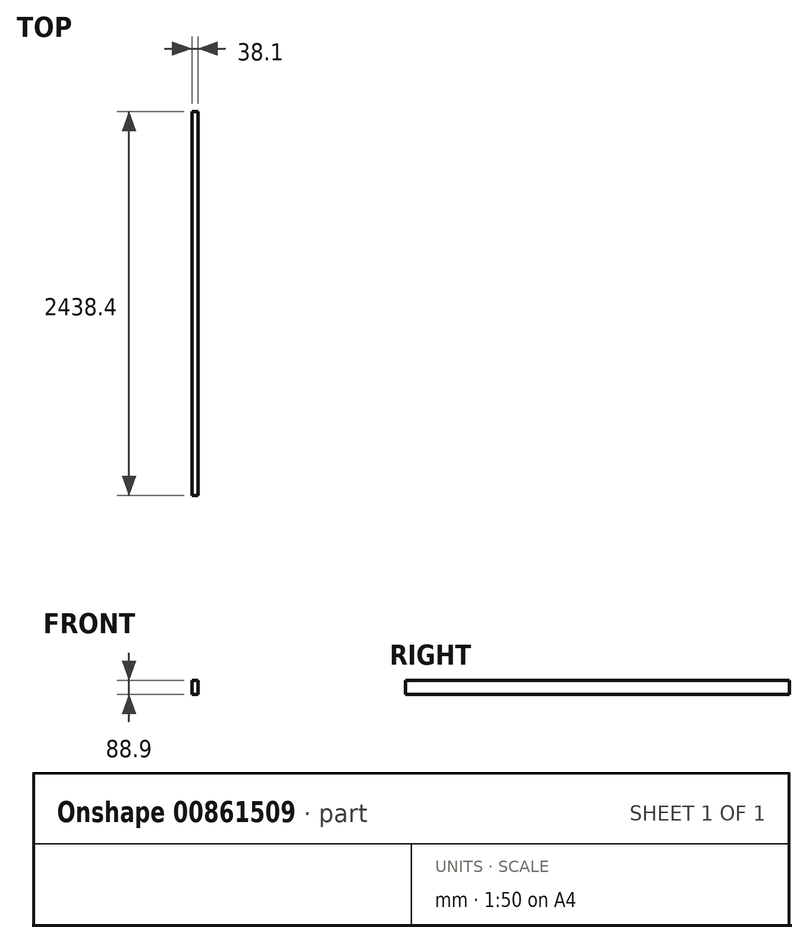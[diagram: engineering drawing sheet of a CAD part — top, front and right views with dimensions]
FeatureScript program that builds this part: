
annotation { "Feature Type Name" : "Feature", "Feature Type Description" : "" }
export const myFeature = defineFeature(function(context is Context, id is Id, definition is map)
    precondition{}
    {
        {
            var Q0;
            Q0=qCreatedBy(makeId("Front.planeOp"),FACE);
            var sketch = newSketch(context, id + "F0", { "sketchPlane" : qUnion([Q0])});
            skLineSegment(sketch, "E0.bottom", {"start": v(-19.05, 44.45) * mm, "end": v(19.05, 44.45) * mm});
            skLineSegment(sketch, "E0.top", {"start": v(-19.05, -44.45) * mm, "end": v(19.05, -44.45) * mm});
            skLineSegment(sketch, "E0.left", {"start": v(-19.05, 44.45) * mm, "end": v(-19.05, -44.45) * mm});
            skLineSegment(sketch, "E0.right", {"start": v(19.05, 44.45) * mm, "end": v(19.05, -44.45) * mm});
            skPoint(sketch, "E0.middle", {"position": v(0, 0) * mm});
            skSolve(sketch);
        }
        {
            var Q0;
            Q0=makeQuery(id+"F0.imprint","IMPRINT",FACE,{"disambiguationData":[TD([[makeQuery(id+"F0.imprint","IMPRINT",EDGE,{"derivedFrom":sQuery(id+"F0.wireOp",EDGE,"E0.bottom")}),-1.0]])]});
            extrude(context, id + "F1", {"entities" : qUnion([Q0]), "depth" : 2438.4 * mm, "offsetDistance" : 25.4 * mm});
        }
    });
